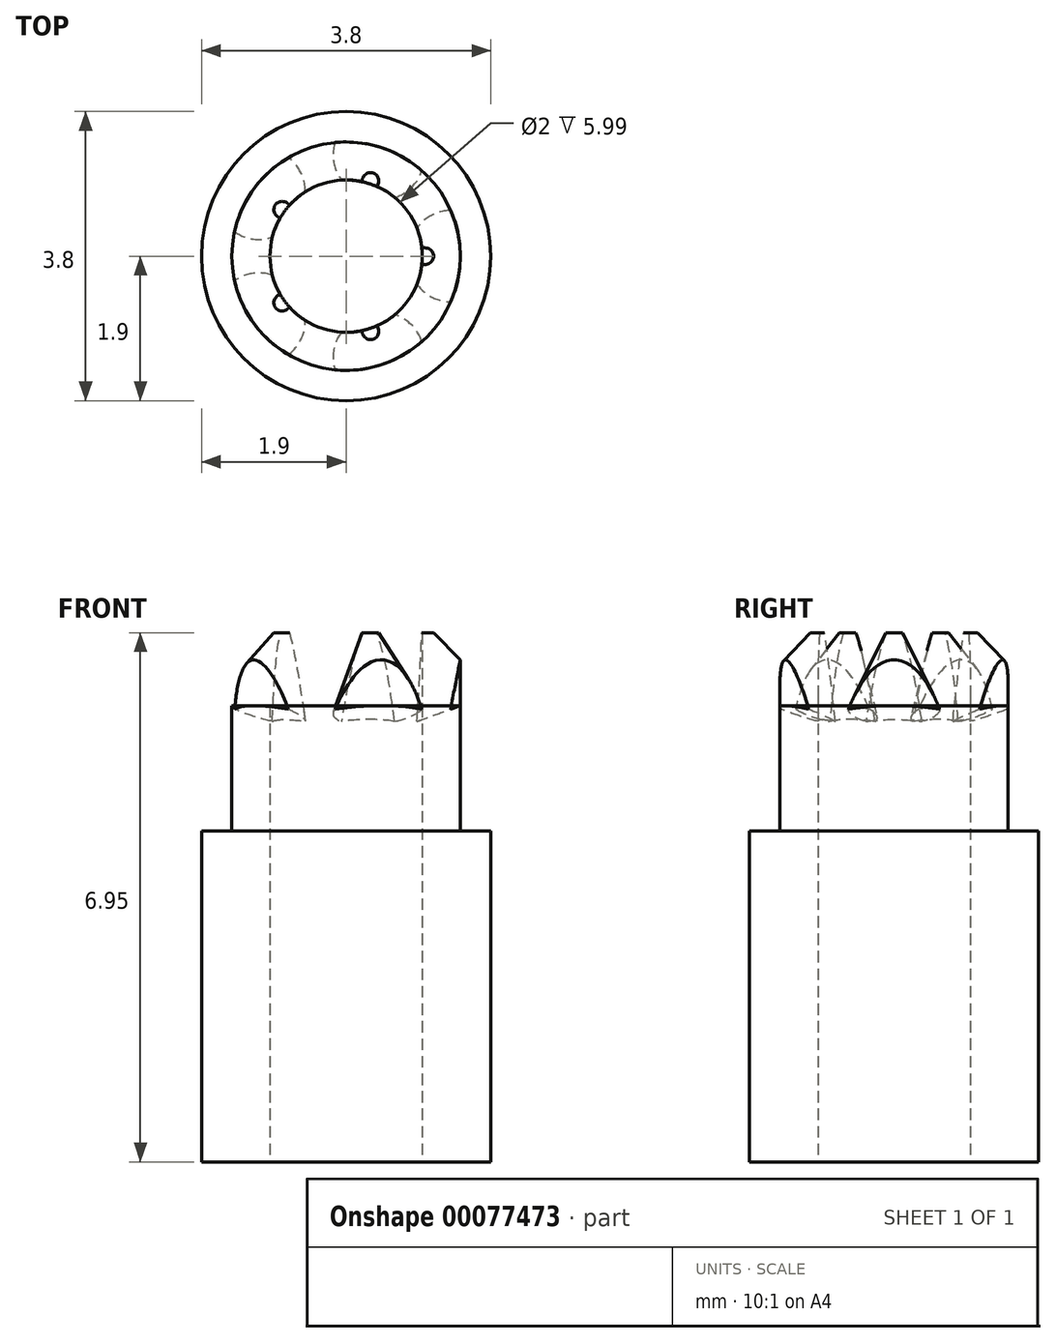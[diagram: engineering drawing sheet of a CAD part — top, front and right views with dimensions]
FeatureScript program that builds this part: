
annotation { "Feature Type Name" : "Feature", "Feature Type Description" : "" }
export const myFeature = defineFeature(function(context is Context, id is Id, definition is map)
    precondition{}
    {
        {
            var Q0;
            Q0=qCreatedBy(makeId("Top.planeOp"),FACE);
            var sketch = newSketch(context, id + "F0", { "sketchPlane" : qUnion([Q0])});
            skCircle(sketch, "E0", {"center": v(0, 0) * mm, "radius": 1 * mm});
            skCircle(sketch, "E1", {"center": v(0, 0) * mm, "radius": 1.5 * mm});
            skCircle(sketch, "E2", {"center": v(0, 0) * mm, "radius": 1.9 * mm});
            skSolve(sketch);
        }
        {
            var Q0;
            Q0=makeQuery(id+"F0.imprint","IMPRINT",FACE,{"disambiguationData":[TD([[makeQuery(id+"F0.imprint","IMPRINT",EDGE,{"derivedFrom":sQuery(id+"F0.wireOp",EDGE,"E0")}),-1.0]])]});
            extrude(context, id + "F1", {"entities" : qUnion([Q0]), "depth" : 2.6 * mm});
        }
        {
            var Q0;
            Q0=qCreatedBy(makeId("Top.planeOp"),FACE);
            cPlane(context, id + "F2", {"entities" : qUnion([Q0]), "cplaneType" : CPlaneType.OFFSET, "offset" : 1.6 * mm, "width" : 150 * mm, "height" : 150 * mm});
        }
        {
            var Q0;
            Q0=qCreatedBy(makeId("Front.planeOp"),FACE);
            var sketch = newSketch(context, id + "F3", { "sketchPlane" : qUnion([Q0])});
            skLineSegment(sketch, "E3", {"start": v(0, 0) * mm, "end": v(0, 1.6) * mm, "construction": true});
            skLineSegment(sketch, "E4", {"start": v(0, 1.6) * mm, "end": v(1.38, 1.6) * mm, "construction": true});
            skLineSegment(sketch, "E5", {"start": v(1.37, 1.6) * mm, "end": v(1.94, 1.8) * mm});
            skLineSegment(sketch, "E6", {"start": v(1.38, 1.6) * mm, "end": v(0.93, 2.82) * mm});
            skLineSegment(sketch, "E7", {"start": v(1.94, 1.8) * mm, "end": v(0.93, 2.82) * mm});
            skSolve(sketch);
        }
        {
            var Q0;
            Q0=makeQuery(id+"F3.imprint","IMPRINT",FACE,{"disambiguationData":[TD([[makeQuery(id+"F3.imprint","IMPRINT",EDGE,{"derivedFrom":sQuery(id+"F3.wireOp",EDGE,"E5")}),1.0]])]});
            var Q1;
            Q1=sQuery(id+"F3.wireOp",EDGE,"E6");
            revolve(context, id + "F4", {"entities" : qUnion([Q0]), "axis" : qUnion([Q1]), "revolveType" : RevolveType.FULL, "oppositeDirection" : true});
        }
        {
            var Q0;
            Q0=makeQuery(id+"F4.opRevolve","SWEPT_BODY",BODY,{"disambiguationData":[OSD([sQuery(id+"F3.wireOp",EDGE,"E5"),sQuery(id+"F3.wireOp",EDGE,"E6"),sQuery(id+"F3.wireOp",EDGE,"E7")])]});
            var Q1;
            Q1=sQuery(id+"F3.wireOp",EDGE,"E3");
            circularPattern(context, id + "F5", {"entities" : qUnion([Q0]), "axis" : qUnion([Q1]), "angle" : 72 * degree, "instanceCount" : round(5)});
        }
        {
            var Q0;
            Q0=makeQuery(id+"F1.opExtrude","SWEPT_BODY",BODY,{"disambiguationData":[OSD([sQuery(id+"F0.wireOp",EDGE,"E0"),sQuery(id+"F0.wireOp",EDGE,"E1")])]});
            transform(context, id + "F6", {"entities" : qUnion([Q0]), "transformType" : TransformType.TRANSLATION_3D, "dx" : 0 * mm, "dy" : 0 * mm, "dz" : 0 * mm, "makeCopy" : true});
        }
        {
            var Q0;
            Q0=makeQuery(id+"F1.opExtrude","SWEPT_BODY",BODY,{"disambiguationData":[OSD([sQuery(id+"F0.wireOp",EDGE,"E0"),sQuery(id+"F0.wireOp",EDGE,"E1")])]});
            var Q1;
            Q1=makeQuery(id+"F4.opRevolve","SWEPT_BODY",BODY,{"disambiguationData":[OSD([sQuery(id+"F3.wireOp",EDGE,"E5"),sQuery(id+"F3.wireOp",EDGE,"E6"),sQuery(id+"F3.wireOp",EDGE,"E7")])]});
            booleanBodies(context, id + "F7", {"operationType" : BooleanOperationType.INTERSECTION, "tools" : qUnion([Q0, Q1])});
        }
        {
            var Q0;
            Q0=makeQuery(id+"F6.opPattern","COPY",BODY,{"derivedFrom":makeQuery(id+"F1.opExtrude","SWEPT_BODY",BODY,{"disambiguationData":[OSD([sQuery(id+"F0.wireOp",EDGE,"E0"),sQuery(id+"F0.wireOp",EDGE,"E1")])]}),"instanceName":"1"});
            transform(context, id + "F8", {"entities" : qUnion([Q0]), "transformType" : TransformType.TRANSLATION_3D, "dx" : 0 * mm, "dy" : 0 * mm, "dz" : 0 * mm, "makeCopy" : true});
        }
        {
            var Q0;
            Q0=makeQuery(id+"F8.opPattern","COPY",BODY,{"derivedFrom":makeQuery(id+"F6.opPattern","COPY",BODY,{"derivedFrom":makeQuery(id+"F1.opExtrude","SWEPT_BODY",BODY,{"disambiguationData":[OSD([sQuery(id+"F0.wireOp",EDGE,"E0"),sQuery(id+"F0.wireOp",EDGE,"E1")])]}),"instanceName":"1"}),"instanceName":"1"});
            transform(context, id + "F9", {"entities" : qUnion([Q0]), "transformType" : TransformType.TRANSLATION_3D, "dx" : 0 * mm, "dy" : 0 * mm, "dz" : 0 * mm, "makeCopy" : true});
        }
        {
            var Q0;
            Q0=makeQuery(id+"F9.opPattern","COPY",BODY,{"derivedFrom":makeQuery(id+"F8.opPattern","COPY",BODY,{"derivedFrom":makeQuery(id+"F6.opPattern","COPY",BODY,{"derivedFrom":makeQuery(id+"F1.opExtrude","SWEPT_BODY",BODY,{"disambiguationData":[OSD([sQuery(id+"F0.wireOp",EDGE,"E0"),sQuery(id+"F0.wireOp",EDGE,"E1")])]}),"instanceName":"1"}),"instanceName":"1"}),"instanceName":"1"});
            transform(context, id + "F10", {"entities" : qUnion([Q0]), "transformType" : TransformType.TRANSLATION_3D, "dx" : 0 * mm, "dy" : 0 * mm, "dz" : 0 * mm, "makeCopy" : true});
        }
        {
            var Q0;
            Q0=makeQuery(id+"F5.opPattern","COPY",BODY,{"derivedFrom":makeQuery(id+"F4.opRevolve","SWEPT_BODY",BODY,{"disambiguationData":[OSD([sQuery(id+"F3.wireOp",EDGE,"E5"),sQuery(id+"F3.wireOp",EDGE,"E6"),sQuery(id+"F3.wireOp",EDGE,"E7")])]}),"instanceName":"1"});
            var Q1;
            Q1=makeQuery(id+"F6.opPattern","COPY",BODY,{"derivedFrom":makeQuery(id+"F1.opExtrude","SWEPT_BODY",BODY,{"disambiguationData":[OSD([sQuery(id+"F0.wireOp",EDGE,"E0"),sQuery(id+"F0.wireOp",EDGE,"E1")])]}),"instanceName":"1"});
            booleanBodies(context, id + "F11", {"operationType" : BooleanOperationType.INTERSECTION, "tools" : qUnion([Q0, Q1])});
        }
        {
            var Q0;
            Q0=makeQuery(id+"F5.opPattern","COPY",BODY,{"derivedFrom":makeQuery(id+"F4.opRevolve","SWEPT_BODY",BODY,{"disambiguationData":[OSD([sQuery(id+"F3.wireOp",EDGE,"E5"),sQuery(id+"F3.wireOp",EDGE,"E6"),sQuery(id+"F3.wireOp",EDGE,"E7")])]}),"instanceName":"2"});
            var Q1;
            Q1=makeQuery(id+"F8.opPattern","COPY",BODY,{"derivedFrom":makeQuery(id+"F6.opPattern","COPY",BODY,{"derivedFrom":makeQuery(id+"F1.opExtrude","SWEPT_BODY",BODY,{"disambiguationData":[OSD([sQuery(id+"F0.wireOp",EDGE,"E0"),sQuery(id+"F0.wireOp",EDGE,"E1")])]}),"instanceName":"1"}),"instanceName":"1"});
            booleanBodies(context, id + "F12", {"operationType" : BooleanOperationType.INTERSECTION, "tools" : qUnion([Q0, Q1])});
        }
        {
            var Q0;
            Q0=makeQuery(id+"F5.opPattern","COPY",BODY,{"derivedFrom":makeQuery(id+"F4.opRevolve","SWEPT_BODY",BODY,{"disambiguationData":[OSD([sQuery(id+"F3.wireOp",EDGE,"E5"),sQuery(id+"F3.wireOp",EDGE,"E6"),sQuery(id+"F3.wireOp",EDGE,"E7")])]}),"instanceName":"3"});
            var Q1;
            Q1=makeQuery(id+"F9.opPattern","COPY",BODY,{"derivedFrom":makeQuery(id+"F8.opPattern","COPY",BODY,{"derivedFrom":makeQuery(id+"F6.opPattern","COPY",BODY,{"derivedFrom":makeQuery(id+"F1.opExtrude","SWEPT_BODY",BODY,{"disambiguationData":[OSD([sQuery(id+"F0.wireOp",EDGE,"E0"),sQuery(id+"F0.wireOp",EDGE,"E1")])]}),"instanceName":"1"}),"instanceName":"1"}),"instanceName":"1"});
            booleanBodies(context, id + "F13", {"operationType" : BooleanOperationType.INTERSECTION, "tools" : qUnion([Q0, Q1])});
        }
        {
            var Q0;
            Q0=makeQuery(id+"F10.opPattern","COPY",BODY,{"derivedFrom":makeQuery(id+"F9.opPattern","COPY",BODY,{"derivedFrom":makeQuery(id+"F8.opPattern","COPY",BODY,{"derivedFrom":makeQuery(id+"F6.opPattern","COPY",BODY,{"derivedFrom":makeQuery(id+"F1.opExtrude","SWEPT_BODY",BODY,{"disambiguationData":[OSD([sQuery(id+"F0.wireOp",EDGE,"E0"),sQuery(id+"F0.wireOp",EDGE,"E1")])]}),"instanceName":"1"}),"instanceName":"1"}),"instanceName":"1"}),"instanceName":"1"});
            transform(context, id + "F14", {"entities" : qUnion([Q0]), "transformType" : TransformType.TRANSLATION_3D, "dx" : 0 * mm, "dy" : 0 * mm, "dz" : 0 * mm, "makeCopy" : true});
        }
        {
            var Q0;
            Q0=makeQuery(id+"F10.opPattern","COPY",BODY,{"derivedFrom":makeQuery(id+"F9.opPattern","COPY",BODY,{"derivedFrom":makeQuery(id+"F8.opPattern","COPY",BODY,{"derivedFrom":makeQuery(id+"F6.opPattern","COPY",BODY,{"derivedFrom":makeQuery(id+"F1.opExtrude","SWEPT_BODY",BODY,{"disambiguationData":[OSD([sQuery(id+"F0.wireOp",EDGE,"E0"),sQuery(id+"F0.wireOp",EDGE,"E1")])]}),"instanceName":"1"}),"instanceName":"1"}),"instanceName":"1"}),"instanceName":"1"});
            var Q1;
            Q1=makeQuery(id+"F5.opPattern","COPY",BODY,{"derivedFrom":makeQuery(id+"F4.opRevolve","SWEPT_BODY",BODY,{"disambiguationData":[OSD([sQuery(id+"F3.wireOp",EDGE,"E5"),sQuery(id+"F3.wireOp",EDGE,"E6"),sQuery(id+"F3.wireOp",EDGE,"E7")])]}),"instanceName":"4"});
            booleanBodies(context, id + "F15", {"operationType" : BooleanOperationType.INTERSECTION, "tools" : qUnion([Q0, Q1])});
        }
        {
            var Q0;
            Q0=makeQuery(id+"F14.opPattern","COPY",BODY,{"derivedFrom":makeQuery(id+"F10.opPattern","COPY",BODY,{"derivedFrom":makeQuery(id+"F9.opPattern","COPY",BODY,{"derivedFrom":makeQuery(id+"F8.opPattern","COPY",BODY,{"derivedFrom":makeQuery(id+"F6.opPattern","COPY",BODY,{"derivedFrom":makeQuery(id+"F1.opExtrude","SWEPT_BODY",BODY,{"disambiguationData":[OSD([sQuery(id+"F0.wireOp",EDGE,"E0"),sQuery(id+"F0.wireOp",EDGE,"E1")])]}),"instanceName":"1"}),"instanceName":"1"}),"instanceName":"1"}),"instanceName":"1"}),"instanceName":"1"});
            deleteBodies(context, id + "F16", {"entities" : qUnion([Q0])});
        }
        {
            var Q0;
            Q0=makeQuery(id+"F0.imprint","IMPRINT",FACE,{"disambiguationData":[TD([[makeQuery(id+"F0.imprint","IMPRINT",EDGE,{"derivedFrom":sQuery(id+"F0.wireOp",EDGE,"E0")}),-1.0]])]});
            extrude(context, id + "F17", {"entities" : qUnion([Q0]), "depth" : 1.64 * mm});
        }
        {
            var Q0;
            Q0=makeQuery(id+"F0.imprint","IMPRINT",FACE,{"disambiguationData":[TD([[makeQuery(id+"F0.imprint","IMPRINT",EDGE,{"derivedFrom":sQuery(id+"F0.wireOp",EDGE,"E1")}),-1.0]])]});
            var Q1;
            Q1=makeQuery(id+"F0.imprint","IMPRINT",FACE,{"disambiguationData":[TD([[makeQuery(id+"F0.imprint","IMPRINT",EDGE,{"derivedFrom":sQuery(id+"F0.wireOp",EDGE,"E0")}),-1.0]])]});
            extrude(context, id + "F18", {"entities" : qUnion([Q0, Q1]), "operationType" : NewBodyOperationType.ADD, "oppositeDirection" : true, "depth" : 4.35 * mm});
        }
    });
